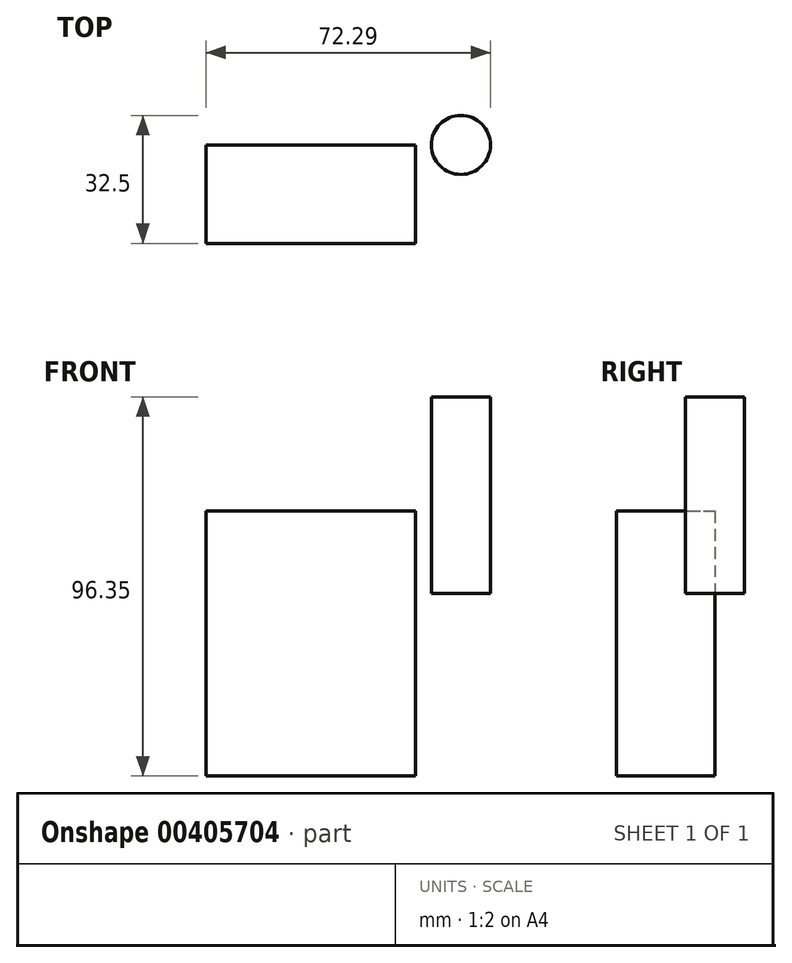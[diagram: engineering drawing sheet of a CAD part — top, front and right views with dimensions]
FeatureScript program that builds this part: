
annotation { "Feature Type Name" : "Feature", "Feature Type Description" : "" }
export const myFeature = defineFeature(function(context is Context, id is Id, definition is map)
    precondition{}
    {
        {
            var Q0;
            Q0=qCreatedBy(makeId("Top.planeOp"),FACE);
            var sketch = newSketch(context, id + "F0", { "sketchPlane" : qUnion([Q0])});
            skCircle(sketch, "E0", {"center": v(0, 0) * mm, "radius": 7.5 * mm});
            skSolve(sketch);
        }
        {
            var Q0;
            Q0=makeQuery(id+"F0.imprint","IMPRINT",FACE,{"disambiguationData":[TD([[makeQuery(id+"F0.imprint","IMPRINT",EDGE,{"derivedFrom":sQuery(id+"F0.wireOp",EDGE,"E0")}),1.0]])]});
            extrude(context, id + "F1", {"entities" : qUnion([Q0]), "depth" : 50 * mm});
        }
        {
            var Q0;
            Q0=qCreatedBy(makeId("Front.planeOp"), FACE);
            var sketch = newSketch(context, id + "F2", { "sketchPlane" : qUnion([Q0]), "disableImprinting" : false});
            skLineSegment(sketch, "E1.bottom", {"start": v(-64.8, 21) * mm, "end": v(-11.52, 21) * mm});
            skLineSegment(sketch, "E1.top", {"start": v(-64.8, -46.35) * mm, "end": v(-11.52, -46.35) * mm});
            skLineSegment(sketch, "E1.left", {"start": v(-64.8, 21) * mm, "end": v(-64.8, -46.35) * mm});
            skLineSegment(sketch, "E1.right", {"start": v(-11.52, 21) * mm, "end": v(-11.52, -46.35) * mm});
            skSolve(sketch);
        }
        {
            var Q0;
            Q0 = qSketchRegion(id + "F2", true);
            extrude(context, id + "F3", {"entities" : qUnion([Q0]), "domain" : OperationDomain.MODEL, "flatOperationType" : FlatOperationType.REMOVE, "depth" : 25 * mm, "offsetDistance" : 25 * mm});
        }
    });
